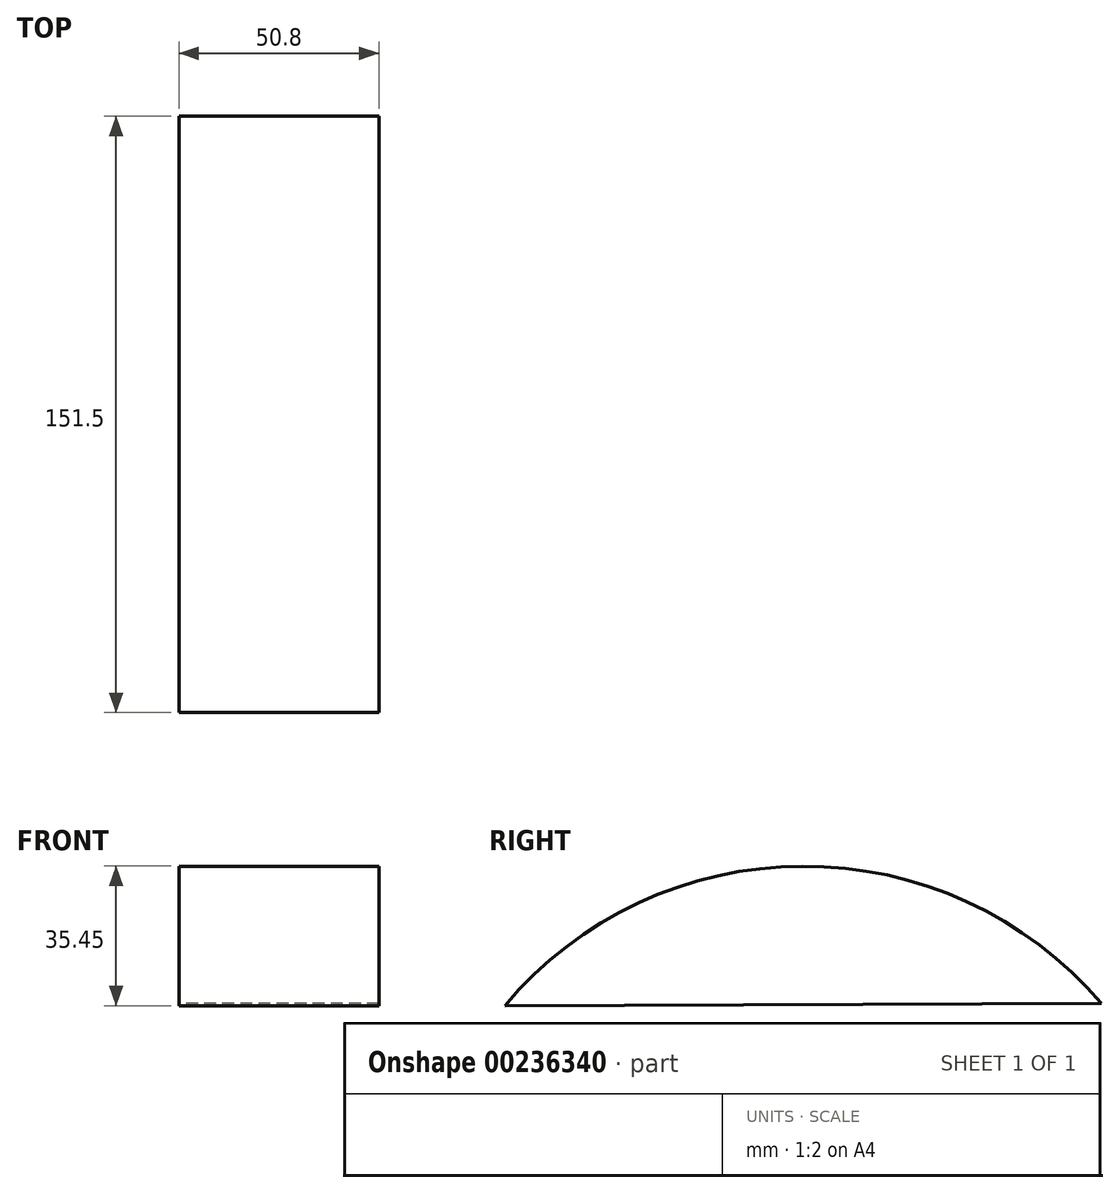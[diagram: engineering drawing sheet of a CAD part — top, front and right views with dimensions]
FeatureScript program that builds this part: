
annotation { "Feature Type Name" : "Feature", "Feature Type Description" : "" }
export const myFeature = defineFeature(function(context is Context, id is Id, definition is map)
    precondition{}
    {
        {
            var Q0;
            Q0=qCreatedBy(makeId("Right.planeOp"),FACE);
            var sketch = newSketch(context, id + "F0", { "sketchPlane" : qUnion([Q0])});
            skLineSegment(sketch, "E0.left", {"start": v(75.51, 64.3) * mm, "end": v(75.51, 0) * mm});
            skLineSegment(sketch, "E0.right", {"start": v(-75.99, 63.73) * mm, "end": v(-75.99, 0) * mm});
            skArc(sketch, "E1.trimOffspring", {"start": v(75.51, 64.3) * mm, "mid": v(-0.37, 99.18) * mm, "end": v(-75.99, 63.73) * mm});
            skLineSegment(sketch, "E2", {"start": v(75.51, 64.3) * mm, "end": v(-75.99, 63.73) * mm});
            skPoint(sketch, "E3.startSnap0", {"position": v(75.51, -5.77) * mm});
            skPoint(sketch, "E4.orphan", {"position": v(75.51, -75.84) * mm});
            skLineSegment(sketch, "E5", {"start": v(0, 64.01) * mm, "end": v(75.51, 0) * mm});
            skLineSegment(sketch, "E6", {"start": v(0, 64.01) * mm, "end": v(-75.99, 0) * mm});
            skSolve(sketch);
        }
        {
            var Q0;
            {var subQ0=sQuery(id+"F0.wireOp",EDGE,"E1.trimOffspring");Q0=makeQuery(id+"F0.imprint","IMPRINT",FACE,{"disambiguationData":[TD([[makeQuery(id+"F0.imprint","IMPRINT",EDGE,{"derivedFrom":subQ0}),1.0]])]});}
            var sketch = newSketch(context, id + "F1", { "sketchPlane" : qUnion([Q0])});
            skSolve(sketch);
        }
        {
            var Q0;
            Q0 = qSketchRegion(id + "F1", true);
            var Q1;
            {var subQ0=sQuery(id+"F0.wireOp",EDGE,"E1.trimOffspring");Q1=makeQuery(id+"F0.imprint","IMPRINT",FACE,{"disambiguationData":[TD([[makeQuery(id+"F0.imprint","IMPRINT",EDGE,{"derivedFrom":subQ0}),1.0]])]});}
            extrude(context, id + "F2", {"entities" : qUnion([Q0, Q1]), "depth" : 50.8 * mm});
        }
    });
